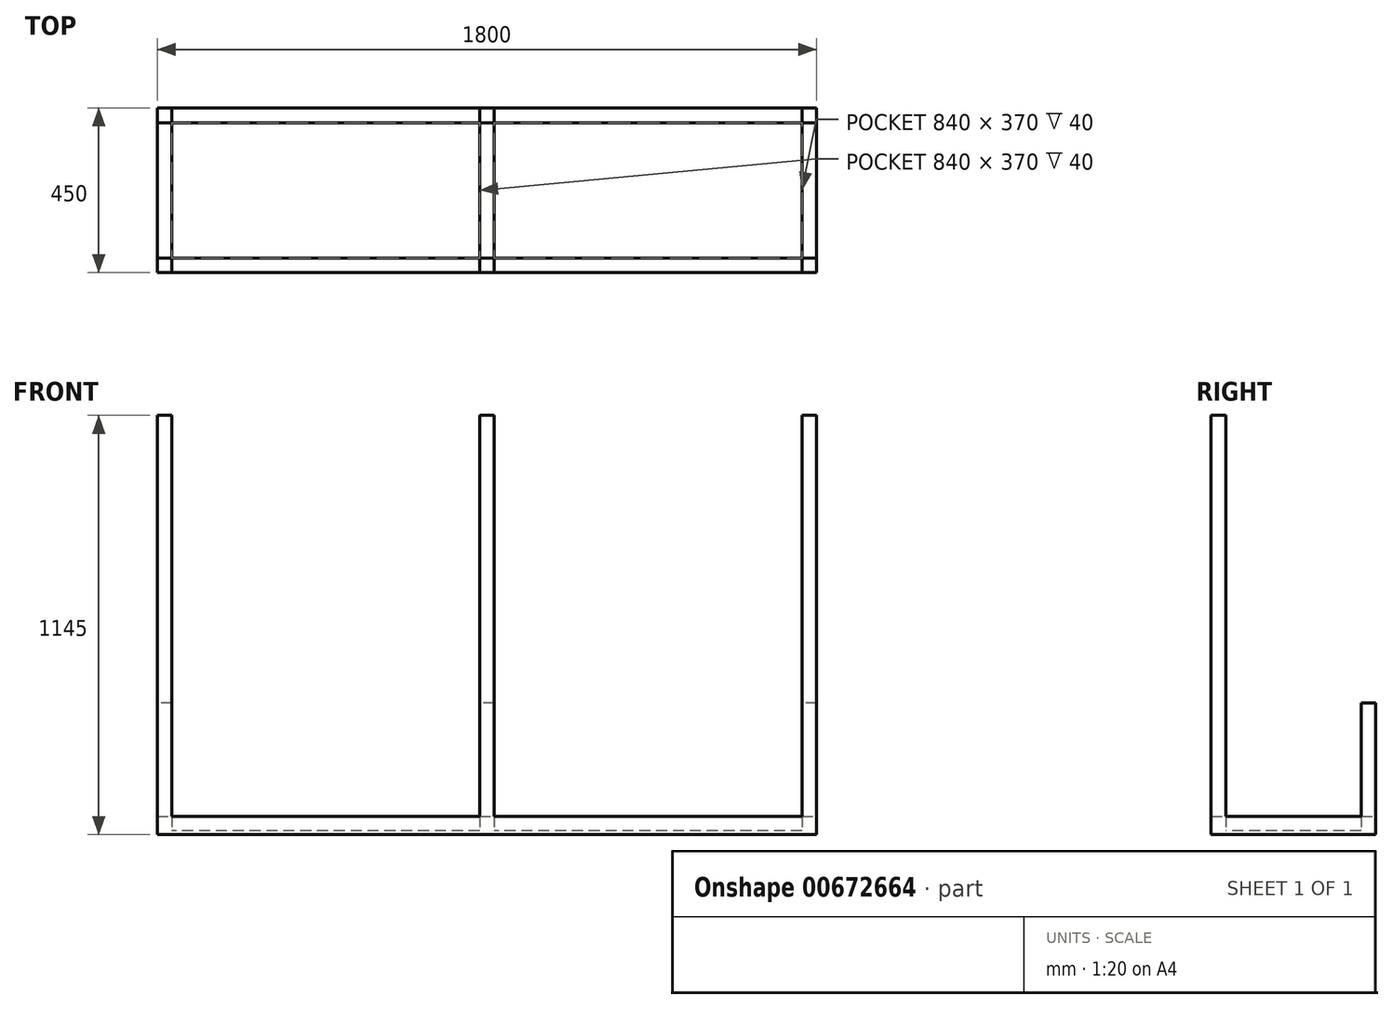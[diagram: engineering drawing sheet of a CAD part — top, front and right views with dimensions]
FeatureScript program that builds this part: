
annotation { "Feature Type Name" : "Feature", "Feature Type Description" : "" }
export const myFeature = defineFeature(function(context is Context, id is Id, definition is map)
    precondition{}
    {
        {
            var Q0;
            Q0=qCreatedBy(makeId("Top.planeOp"),FACE);
            var sketch = newSketch(context, id + "F0", { "sketchPlane" : qUnion([Q0])});
            skLineSegment(sketch, "E0.bottom", {"start": v(900, -225) * mm, "end": v(-900, -225) * mm});
            skLineSegment(sketch, "E0.top", {"start": v(900, 225) * mm, "end": v(-900, 225) * mm});
            skLineSegment(sketch, "E0.left", {"start": v(900, -225) * mm, "end": v(900, 225) * mm});
            skLineSegment(sketch, "E0.right", {"start": v(-900, -225) * mm, "end": v(-900, 225) * mm});
            skPoint(sketch, "E0.middle", {"position": v(0, 0) * mm});
            skSolve(sketch);
        }
        {
            var Q0;
            Q0=makeQuery(id+"F0.imprint","IMPRINT",FACE,{"disambiguationData":[TD([[makeQuery(id+"F0.imprint","IMPRINT",EDGE,{"derivedFrom":sQuery(id+"F0.wireOp",EDGE,"E0.bottom")}),-1.0]])]});
            extrude(context, id + "F1", {"entities" : qUnion([Q0]), "depth" : 10 * mm, "offsetDistance" : 25 * mm});
        }
        {
            var Q0;
            Q0=makeQuery(id+"F1.opExtrude","CAP_FACE",FACE,{"disambiguationData":[OSD([sQuery(id+"F0.wireOp",EDGE,"E0.bottom"),sQuery(id+"F0.wireOp",EDGE,"E0.top"),sQuery(id+"F0.wireOp",EDGE,"E0.left"),sQuery(id+"F0.wireOp",EDGE,"E0.right")])],"isStart":false});
            var sketch = newSketch(context, id + "F2", { "sketchPlane" : qUnion([Q0])});
            skLineSegment(sketch, "E1.bottom", {"start": v(-900, 225) * mm, "end": v(-860, 225) * mm});
            skLineSegment(sketch, "E1.top", {"start": v(-900, -225) * mm, "end": v(-860, -225) * mm});
            skLineSegment(sketch, "E1.left", {"start": v(-900, 225) * mm, "end": v(-900, -225) * mm});
            skLineSegment(sketch, "E1.right", {"start": v(-860, 225) * mm, "end": v(-860, -225) * mm});
            skSolve(sketch);
        }
        {
            var Q0;
            Q0=makeQuery(id+"F2.imprint","IMPRINT",FACE,{"disambiguationData":[TD([[makeQuery(id+"F2.imprint","IMPRINT",EDGE,{"derivedFrom":sQuery(id+"F2.wireOp",EDGE,"E1.bottom")}),1.0]])]});
            extrude(context, id + "F3", {"entities" : qUnion([Q0]), "operationType" : NewBodyOperationType.ADD, "depth" : 40 * mm, "offsetDistance" : 25 * mm});
        }
        {
            var Q0;
            Q0=makeQuery(id+"F1.opExtrude","CAP_FACE",FACE,{"disambiguationData":[OSD([sQuery(id+"F0.wireOp",EDGE,"E0.bottom"),sQuery(id+"F0.wireOp",EDGE,"E0.top"),sQuery(id+"F0.wireOp",EDGE,"E0.left"),sQuery(id+"F0.wireOp",EDGE,"E0.right")])],"isStart":false});
            var sketch = newSketch(context, id + "F4", { "sketchPlane" : qUnion([Q0])});
            skLineSegment(sketch, "E2.bottom", {"start": v(900, 225) * mm, "end": v(860, 225) * mm});
            skLineSegment(sketch, "E2.top", {"start": v(900, -225) * mm, "end": v(860, -225) * mm});
            skLineSegment(sketch, "E2.left", {"start": v(900, 225) * mm, "end": v(900, -225) * mm});
            skLineSegment(sketch, "E2.right", {"start": v(860, 225) * mm, "end": v(860, -225) * mm});
            skSolve(sketch);
        }
        {
            var Q0;
            Q0=makeQuery(id+"F4.imprint","IMPRINT",FACE,{"disambiguationData":[TD([[makeQuery(id+"F4.imprint","IMPRINT",EDGE,{"derivedFrom":sQuery(id+"F4.wireOp",EDGE,"E2.bottom")}),1.0]])]});
            extrude(context, id + "F5", {"entities" : qUnion([Q0]), "operationType" : NewBodyOperationType.ADD, "depth" : 40 * mm, "offsetDistance" : 25 * mm});
        }
        {
            var Q0;
            Q0=makeQuery(id+"F1.opExtrude","CAP_FACE",FACE,{"disambiguationData":[OSD([sQuery(id+"F0.wireOp",EDGE,"E0.bottom"),sQuery(id+"F0.wireOp",EDGE,"E0.top"),sQuery(id+"F0.wireOp",EDGE,"E0.left"),sQuery(id+"F0.wireOp",EDGE,"E0.right")])],"isStart":false});
            var sketch = newSketch(context, id + "F6", { "sketchPlane" : qUnion([Q0])});
            skLineSegment(sketch, "E3.bottom", {"start": v(-20, 185) * mm, "end": v(20, 185) * mm});
            skLineSegment(sketch, "E3.top", {"start": v(-20, -185) * mm, "end": v(20, -185) * mm});
            skLineSegment(sketch, "E3.left", {"start": v(-20, 185) * mm, "end": v(-20, -185) * mm});
            skLineSegment(sketch, "E3.right", {"start": v(20, 185) * mm, "end": v(20, -185) * mm});
            skPoint(sketch, "E3.middle", {"position": v(0, 0) * mm});
            skSolve(sketch);
        }
        {
            var Q0;
            Q0=makeQuery(id+"F6.imprint","IMPRINT",FACE,{"disambiguationData":[TD([[makeQuery(id+"F6.imprint","IMPRINT",EDGE,{"derivedFrom":sQuery(id+"F6.wireOp",EDGE,"E3.bottom")}),-1.0]])]});
            extrude(context, id + "F7", {"entities" : qUnion([Q0]), "operationType" : NewBodyOperationType.ADD, "depth" : 40 * mm, "offsetDistance" : 25 * mm});
        }
        {
            var Q0;
            Q0=makeQuery(id+"F1.opExtrude","CAP_FACE",FACE,{"disambiguationData":[OSD([sQuery(id+"F0.wireOp",EDGE,"E0.bottom"),sQuery(id+"F0.wireOp",EDGE,"E0.top"),sQuery(id+"F0.wireOp",EDGE,"E0.left"),sQuery(id+"F0.wireOp",EDGE,"E0.right")])],"isStart":false});
            var sketch = newSketch(context, id + "F8", { "sketchPlane" : qUnion([Q0])});
            skLineSegment(sketch, "E4.bottom", {"start": v(860, -225) * mm, "end": v(-860, -225) * mm});
            skLineSegment(sketch, "E4.top", {"start": v(860, -185) * mm, "end": v(-860, -185) * mm});
            skLineSegment(sketch, "E4.left", {"start": v(860, -225) * mm, "end": v(860, -185) * mm});
            skLineSegment(sketch, "E4.right", {"start": v(-860, -225) * mm, "end": v(-860, -185) * mm});
            skSolve(sketch);
        }
        {
            var Q0;
            Q0=makeQuery(id+"F8.imprint","IMPRINT",FACE,{"disambiguationData":[TD([[makeQuery(id+"F8.imprint","IMPRINT",EDGE,{"derivedFrom":sQuery(id+"F8.wireOp",EDGE,"E4.bottom")}),-1.0]])]});
            extrude(context, id + "F9", {"entities" : qUnion([Q0]), "operationType" : NewBodyOperationType.ADD, "depth" : 40 * mm, "offsetDistance" : 25 * mm});
        }
        {
            var Q0;
            Q0=makeQuery(id+"F1.opExtrude","CAP_FACE",FACE,{"disambiguationData":[OSD([sQuery(id+"F0.wireOp",EDGE,"E0.bottom"),sQuery(id+"F0.wireOp",EDGE,"E0.top"),sQuery(id+"F0.wireOp",EDGE,"E0.left"),sQuery(id+"F0.wireOp",EDGE,"E0.right")])],"isStart":false});
            var sketch = newSketch(context, id + "F10", { "sketchPlane" : qUnion([Q0])});
            skLineSegment(sketch, "E5.bottom", {"start": v(860, 225) * mm, "end": v(-860, 225) * mm});
            skLineSegment(sketch, "E5.top", {"start": v(860, 185) * mm, "end": v(-860, 185) * mm});
            skLineSegment(sketch, "E5.left", {"start": v(860, 225) * mm, "end": v(860, 185) * mm});
            skLineSegment(sketch, "E5.right", {"start": v(-860, 225) * mm, "end": v(-860, 185) * mm});
            skSolve(sketch);
        }
        {
            var Q0;
            Q0=makeQuery(id+"F10.imprint","IMPRINT",FACE,{"disambiguationData":[TD([[makeQuery(id+"F10.imprint","IMPRINT",EDGE,{"derivedFrom":sQuery(id+"F10.wireOp",EDGE,"E5.bottom")}),1.0]])]});
            extrude(context, id + "F11", {"entities" : qUnion([Q0]), "operationType" : NewBodyOperationType.ADD, "depth" : 40 * mm, "offsetDistance" : 25 * mm});
        }
        {
            var Q0;
            Q0=makeQuery(id+"F11.boolean.opBoolean","MERGE",FACE,{"derivedFrom":[makeQuery(id+"F9.boolean.opBoolean","MERGE",FACE,{"derivedFrom":[makeQuery(id+"F3.opExtrude","CAP_FACE",FACE,{"disambiguationData":[OSD([sQuery(id+"F2.wireOp",EDGE,"E1.bottom"),sQuery(id+"F2.wireOp",EDGE,"E1.top"),sQuery(id+"F2.wireOp",EDGE,"E1.left"),sQuery(id+"F2.wireOp",EDGE,"E1.right")])],"isStart":false}),makeQuery(id+"F5.opExtrude","CAP_FACE",FACE,{"disambiguationData":[OSD([sQuery(id+"F4.wireOp",EDGE,"E2.bottom"),sQuery(id+"F4.wireOp",EDGE,"E2.top"),sQuery(id+"F4.wireOp",EDGE,"E2.left"),sQuery(id+"F4.wireOp",EDGE,"E2.right")])],"isStart":false}),makeQuery(id+"F7.opExtrude","CAP_FACE",FACE,{"disambiguationData":[OSD([sQuery(id+"F6.wireOp",EDGE,"E3.bottom"),sQuery(id+"F6.wireOp",EDGE,"E3.top"),sQuery(id+"F6.wireOp",EDGE,"E3.left"),sQuery(id+"F6.wireOp",EDGE,"E3.right")])],"isStart":false}),makeQuery(id+"F9.opExtrude","CAP_FACE",FACE,{"disambiguationData":[OSD([sQuery(id+"F8.wireOp",EDGE,"E4.bottom"),sQuery(id+"F8.wireOp",EDGE,"E4.top"),sQuery(id+"F8.wireOp",EDGE,"E4.left"),sQuery(id+"F8.wireOp",EDGE,"E4.right")])],"isStart":false})]}),makeQuery(id+"F11.opExtrude","CAP_FACE",FACE,{"disambiguationData":[OSD([sQuery(id+"F10.wireOp",EDGE,"E5.bottom"),sQuery(id+"F10.wireOp",EDGE,"E5.top"),sQuery(id+"F10.wireOp",EDGE,"E5.left"),sQuery(id+"F10.wireOp",EDGE,"E5.right")])],"isStart":false})]});
            var sketch = newSketch(context, id + "F12", { "sketchPlane" : qUnion([Q0])});
            skLineSegment(sketch, "E6.bottom", {"start": v(-900, -225) * mm, "end": v(-860, -225) * mm});
            skLineSegment(sketch, "E6.top", {"start": v(-900, -185) * mm, "end": v(-860, -185) * mm});
            skLineSegment(sketch, "E6.left", {"start": v(-900, -225) * mm, "end": v(-900, -185) * mm});
            skLineSegment(sketch, "E6.right", {"start": v(-860, -225) * mm, "end": v(-860, -185) * mm});
            skSolve(sketch);
        }
        {
            var Q0;
            Q0=makeQuery(id+"F12.imprint","IMPRINT",FACE,{"disambiguationData":[TD([[makeQuery(id+"F12.imprint","IMPRINT",EDGE,{"derivedFrom":sQuery(id+"F12.wireOp",EDGE,"E6.bottom")}),-1.0]])]});
            extrude(context, id + "F13", {"entities" : qUnion([Q0]), "operationType" : NewBodyOperationType.ADD, "depth" : 1095 * mm, "offsetDistance" : 25 * mm});
        }
        {
            var Q0;
            Q0=makeQuery(id+"F11.boolean.opBoolean","MERGE",FACE,{"derivedFrom":[makeQuery(id+"F9.boolean.opBoolean","MERGE",FACE,{"derivedFrom":[makeQuery(id+"F3.opExtrude","CAP_FACE",FACE,{"disambiguationData":[OSD([sQuery(id+"F2.wireOp",EDGE,"E1.bottom"),sQuery(id+"F2.wireOp",EDGE,"E1.top"),sQuery(id+"F2.wireOp",EDGE,"E1.left"),sQuery(id+"F2.wireOp",EDGE,"E1.right")])],"isStart":false}),makeQuery(id+"F5.opExtrude","CAP_FACE",FACE,{"disambiguationData":[OSD([sQuery(id+"F4.wireOp",EDGE,"E2.bottom"),sQuery(id+"F4.wireOp",EDGE,"E2.top"),sQuery(id+"F4.wireOp",EDGE,"E2.left"),sQuery(id+"F4.wireOp",EDGE,"E2.right")])],"isStart":false}),makeQuery(id+"F7.opExtrude","CAP_FACE",FACE,{"disambiguationData":[OSD([sQuery(id+"F6.wireOp",EDGE,"E3.bottom"),sQuery(id+"F6.wireOp",EDGE,"E3.top"),sQuery(id+"F6.wireOp",EDGE,"E3.left"),sQuery(id+"F6.wireOp",EDGE,"E3.right")])],"isStart":false}),makeQuery(id+"F9.opExtrude","CAP_FACE",FACE,{"disambiguationData":[OSD([sQuery(id+"F8.wireOp",EDGE,"E4.bottom"),sQuery(id+"F8.wireOp",EDGE,"E4.top"),sQuery(id+"F8.wireOp",EDGE,"E4.left"),sQuery(id+"F8.wireOp",EDGE,"E4.right")])],"isStart":false})]}),makeQuery(id+"F11.opExtrude","CAP_FACE",FACE,{"disambiguationData":[OSD([sQuery(id+"F10.wireOp",EDGE,"E5.bottom"),sQuery(id+"F10.wireOp",EDGE,"E5.top"),sQuery(id+"F10.wireOp",EDGE,"E5.left"),sQuery(id+"F10.wireOp",EDGE,"E5.right")])],"isStart":false})]});
            var sketch = newSketch(context, id + "F14", { "sketchPlane" : qUnion([Q0])});
            skLineSegment(sketch, "E7.bottom", {"start": v(-20, -185) * mm, "end": v(20, -185) * mm});
            skLineSegment(sketch, "E7.top", {"start": v(-20, -225) * mm, "end": v(20, -225) * mm});
            skLineSegment(sketch, "E7.left", {"start": v(-20, -185) * mm, "end": v(-20, -225) * mm});
            skLineSegment(sketch, "E7.right", {"start": v(20, -185) * mm, "end": v(20, -225) * mm});
            skSolve(sketch);
        }
        {
            var Q0;
            Q0=makeQuery(id+"F14.imprint","IMPRINT",FACE,{"disambiguationData":[TD([[makeQuery(id+"F14.imprint","IMPRINT",EDGE,{"derivedFrom":sQuery(id+"F14.wireOp",EDGE,"E7.bottom")}),-1.0]])]});
            extrude(context, id + "F15", {"entities" : qUnion([Q0]), "operationType" : NewBodyOperationType.ADD, "depth" : 1095 * mm, "offsetDistance" : 25 * mm});
        }
        {
            var Q0;
            {var subQ0=sQuery(id+"F10.wireOp",EDGE,"E5.bottom");var subQ1=sQuery(id+"F10.wireOp",EDGE,"E5.top");var subQ2=makeQuery(id+"F11.opExtrude","CAP_FACE",FACE,{"disambiguationData":[OSD([subQ0,subQ1,sQuery(id+"F10.wireOp",EDGE,"E5.left"),sQuery(id+"F10.wireOp",EDGE,"E5.right")])],"isStart":false});var subQ3=sQuery(id+"F6.wireOp",EDGE,"E3.right");var subQ4=sQuery(id+"F6.wireOp",EDGE,"E3.left");var subQ5=sQuery(id+"F8.wireOp",EDGE,"E4.top");var subQ6=sQuery(id+"F8.wireOp",EDGE,"E4.bottom");var subQ7=makeQuery(id+"F9.opExtrude","CAP_FACE",FACE,{"disambiguationData":[OSD([subQ6,subQ5,sQuery(id+"F8.wireOp",EDGE,"E4.left"),sQuery(id+"F8.wireOp",EDGE,"E4.right")])],"isStart":false});var subQ8=sQuery(id+"F4.wireOp",EDGE,"E2.right");var subQ9=sQuery(id+"F4.wireOp",EDGE,"E2.left");var subQ10=sQuery(id+"F4.wireOp",EDGE,"E2.top");var subQ11=sQuery(id+"F4.wireOp",EDGE,"E2.bottom");var subQ12=makeQuery(id+"F5.opExtrude","CAP_FACE",FACE,{"disambiguationData":[OSD([subQ11,subQ10,subQ9,subQ8])],"isStart":false});var subQ13=sQuery(id+"F2.wireOp",EDGE,"E1.top");var subQ14=sQuery(id+"F2.wireOp",EDGE,"E1.right");var subQ15=sQuery(id+"F2.wireOp",EDGE,"E1.left");var subQ16=sQuery(id+"F2.wireOp",EDGE,"E1.bottom");var subQ17=makeQuery(id+"F3.opExtrude","CAP_FACE",FACE,{"disambiguationData":[OSD([subQ16,subQ13,subQ15,subQ14])],"isStart":false});var subQ18=makeQuery(id+"F7.opExtrude","CAP_FACE",FACE,{"disambiguationData":[OSD([sQuery(id+"F6.wireOp",EDGE,"E3.bottom"),sQuery(id+"F6.wireOp",EDGE,"E3.top"),subQ4,subQ3])],"isStart":false});Q0=makeQuery(id+"F15.boolean.opBoolean","SPLIT",FACE,{"disambiguationData":[TD([makeQuery(id+"F1.opExtrude","SWEPT_FACE",FACE,{"disambiguationData":[OSD([sQuery(id+"F0.wireOp",EDGE,"E0.bottom")])]}),makeQuery(id+"F1.opExtrude","SWEPT_FACE",FACE,{"disambiguationData":[OSD([sQuery(id+"F0.wireOp",EDGE,"E0.top")])]}),makeQuery(id+"F1.opExtrude","SWEPT_FACE",FACE,{"disambiguationData":[OSD([sQuery(id+"F0.wireOp",EDGE,"E0.left")])]}),makeQuery(id+"F1.opExtrude","SWEPT_FACE",FACE,{"disambiguationData":[OSD([sQuery(id+"F0.wireOp",EDGE,"E0.right")])]}),makeQuery(id+"F3.opExtrude","SWEPT_FACE",FACE,{"disambiguationData":[OSD([subQ16])]}),subQ17,makeQuery(id+"F3.opExtrude","SWEPT_FACE",FACE,{"disambiguationData":[OSD([subQ13])]}),makeQuery(id+"F3.opExtrude","SWEPT_FACE",FACE,{"disambiguationData":[OSD([subQ15])]}),makeQuery(id+"F3.opExtrude","SWEPT_FACE",FACE,{"disambiguationData":[OSD([subQ14])]}),makeQuery(id+"F5.opExtrude","SWEPT_FACE",FACE,{"disambiguationData":[OSD([subQ11])]}),subQ12,makeQuery(id+"F5.opExtrude","SWEPT_FACE",FACE,{"disambiguationData":[OSD([subQ10])]}),makeQuery(id+"F5.opExtrude","SWEPT_FACE",FACE,{"disambiguationData":[OSD([subQ9])]}),makeQuery(id+"F5.opExtrude","SWEPT_FACE",FACE,{"disambiguationData":[OSD([subQ8])]}),subQ18,makeQuery(id+"F7.opExtrude","SWEPT_FACE",FACE,{"disambiguationData":[OSD([subQ4])]}),makeQuery(id+"F7.opExtrude","SWEPT_FACE",FACE,{"disambiguationData":[OSD([subQ3])]}),makeQuery(id+"F9.opExtrude","SWEPT_FACE",FACE,{"disambiguationData":[OSD([subQ6])]}),subQ7,makeQuery(id+"F9.opExtrude","SWEPT_FACE",FACE,{"disambiguationData":[OSD([subQ5])]}),makeQuery(id+"F11.opExtrude","SWEPT_FACE",FACE,{"disambiguationData":[OSD([subQ0])]}),subQ2,makeQuery(id+"F11.opExtrude","SWEPT_FACE",FACE,{"disambiguationData":[OSD([subQ1])]}),makeQuery(id+"F13.opExtrude","SWEPT_FACE",FACE,{"disambiguationData":[OSD([sQuery(id+"F12.wireOp",EDGE,"E6.bottom")])]}),makeQuery(id+"F13.opExtrude","SWEPT_FACE",FACE,{"disambiguationData":[OSD([sQuery(id+"F12.wireOp",EDGE,"E6.top")])]}),makeQuery(id+"F13.opExtrude","SWEPT_FACE",FACE,{"disambiguationData":[OSD([sQuery(id+"F12.wireOp",EDGE,"E6.left")])]}),makeQuery(id+"F13.opExtrude","SWEPT_FACE",FACE,{"disambiguationData":[OSD([sQuery(id+"F12.wireOp",EDGE,"E6.right")])]}),makeQuery(id+"F15.opExtrude","SWEPT_FACE",FACE,{"disambiguationData":[OSD([sQuery(id+"F14.wireOp",EDGE,"E7.bottom")])]}),makeQuery(id+"F15.opExtrude","SWEPT_FACE",FACE,{"disambiguationData":[OSD([sQuery(id+"F14.wireOp",EDGE,"E7.top")])]}),makeQuery(id+"F15.opExtrude","SWEPT_FACE",FACE,{"disambiguationData":[OSD([sQuery(id+"F14.wireOp",EDGE,"E7.left")])]}),makeQuery(id+"F15.opExtrude","SWEPT_FACE",FACE,{"disambiguationData":[OSD([sQuery(id+"F14.wireOp",EDGE,"E7.right")])]})])],"derivedFrom":makeQuery(id+"F11.boolean.opBoolean","MERGE",FACE,{"derivedFrom":[makeQuery(id+"F9.boolean.opBoolean","MERGE",FACE,{"derivedFrom":[subQ17,subQ12,subQ18,subQ7]}),subQ2]})});}
            var sketch = newSketch(context, id + "F16", { "sketchPlane" : qUnion([Q0])});
            skLineSegment(sketch, "E8.bottom", {"start": v(900, -225) * mm, "end": v(860, -225) * mm});
            skLineSegment(sketch, "E8.top", {"start": v(900, -185) * mm, "end": v(860, -185) * mm});
            skLineSegment(sketch, "E8.left", {"start": v(900, -225) * mm, "end": v(900, -185) * mm});
            skLineSegment(sketch, "E8.right", {"start": v(860, -225) * mm, "end": v(860, -185) * mm});
            skSolve(sketch);
        }
        {
            var Q0;
            Q0=makeQuery(id+"F16.imprint","IMPRINT",FACE,{"disambiguationData":[TD([[makeQuery(id+"F16.imprint","IMPRINT",EDGE,{"derivedFrom":sQuery(id+"F16.wireOp",EDGE,"E8.bottom")}),-1.0]])]});
            extrude(context, id + "F17", {"entities" : qUnion([Q0]), "operationType" : NewBodyOperationType.ADD, "depth" : 1095 * mm, "offsetDistance" : 25 * mm});
        }
        {
            var Q0;
            {var subQ0=sQuery(id+"F10.wireOp",EDGE,"E5.top");var subQ1=makeQuery(id+"F11.opExtrude","SWEPT_FACE",FACE,{"disambiguationData":[OSD([subQ0])]});var subQ2=sQuery(id+"F10.wireOp",EDGE,"E5.bottom");var subQ3=makeQuery(id+"F11.opExtrude","SWEPT_FACE",FACE,{"disambiguationData":[OSD([subQ2])]});var subQ4=makeQuery(id+"F1.opExtrude","SWEPT_FACE",FACE,{"disambiguationData":[OSD([sQuery(id+"F0.wireOp",EDGE,"E0.right")])]});var subQ5=sQuery(id+"F8.wireOp",EDGE,"E4.top");var subQ6=makeQuery(id+"F9.opExtrude","SWEPT_FACE",FACE,{"disambiguationData":[OSD([subQ5])]});var subQ7=makeQuery(id+"F11.opExtrude","CAP_FACE",FACE,{"disambiguationData":[OSD([subQ2,subQ0,sQuery(id+"F10.wireOp",EDGE,"E5.left"),sQuery(id+"F10.wireOp",EDGE,"E5.right")])],"isStart":false});var subQ8=sQuery(id+"F6.wireOp",EDGE,"E3.right");var subQ9=makeQuery(id+"F7.opExtrude","SWEPT_FACE",FACE,{"disambiguationData":[OSD([subQ8])]});var subQ10=sQuery(id+"F6.wireOp",EDGE,"E3.left");var subQ11=makeQuery(id+"F7.opExtrude","SWEPT_FACE",FACE,{"disambiguationData":[OSD([subQ10])]});var subQ12=sQuery(id+"F8.wireOp",EDGE,"E4.bottom");var subQ13=makeQuery(id+"F9.opExtrude","CAP_FACE",FACE,{"disambiguationData":[OSD([subQ12,subQ5,sQuery(id+"F8.wireOp",EDGE,"E4.left"),sQuery(id+"F8.wireOp",EDGE,"E4.right")])],"isStart":false});var subQ14=sQuery(id+"F4.wireOp",EDGE,"E2.right");var subQ15=makeQuery(id+"F5.opExtrude","SWEPT_FACE",FACE,{"disambiguationData":[OSD([subQ14])]});var subQ16=makeQuery(id+"F13.opExtrude","SWEPT_FACE",FACE,{"disambiguationData":[OSD([sQuery(id+"F12.wireOp",EDGE,"E6.right")])]});var subQ17=sQuery(id+"F2.wireOp",EDGE,"E1.left");var subQ18=makeQuery(id+"F3.opExtrude","SWEPT_FACE",FACE,{"disambiguationData":[OSD([subQ17])]});var subQ19=makeQuery(id+"F13.opExtrude","SWEPT_FACE",FACE,{"disambiguationData":[OSD([sQuery(id+"F12.wireOp",EDGE,"E6.left")])]});var subQ20=makeQuery(id+"F1.opExtrude","SWEPT_FACE",FACE,{"disambiguationData":[OSD([sQuery(id+"F0.wireOp",EDGE,"E0.left")])]});var subQ21=sQuery(id+"F2.wireOp",EDGE,"E1.bottom");var subQ22=makeQuery(id+"F3.opExtrude","SWEPT_FACE",FACE,{"disambiguationData":[OSD([subQ21])]});var subQ23=makeQuery(id+"F13.opExtrude","SWEPT_FACE",FACE,{"disambiguationData":[OSD([sQuery(id+"F12.wireOp",EDGE,"E6.top")])]});var subQ24=makeQuery(id+"F1.opExtrude","SWEPT_FACE",FACE,{"disambiguationData":[OSD([sQuery(id+"F0.wireOp",EDGE,"E0.top")])]});var subQ25=sQuery(id+"F2.wireOp",EDGE,"E1.right");var subQ26=sQuery(id+"F2.wireOp",EDGE,"E1.top");var subQ27=makeQuery(id+"F3.opExtrude","CAP_FACE",FACE,{"disambiguationData":[OSD([subQ21,subQ26,subQ17,subQ25])],"isStart":false});var subQ28=makeQuery(id+"F7.opExtrude","CAP_FACE",FACE,{"disambiguationData":[OSD([sQuery(id+"F6.wireOp",EDGE,"E3.bottom"),sQuery(id+"F6.wireOp",EDGE,"E3.top"),subQ10,subQ8])],"isStart":false});var subQ29=makeQuery(id+"F3.opExtrude","SWEPT_FACE",FACE,{"disambiguationData":[OSD([subQ25])]});var subQ30=sQuery(id+"F4.wireOp",EDGE,"E2.bottom");var subQ31=makeQuery(id+"F5.opExtrude","SWEPT_FACE",FACE,{"disambiguationData":[OSD([subQ30])]});var subQ32=sQuery(id+"F4.wireOp",EDGE,"E2.left");var subQ33=sQuery(id+"F4.wireOp",EDGE,"E2.top");var subQ34=makeQuery(id+"F5.opExtrude","CAP_FACE",FACE,{"disambiguationData":[OSD([subQ30,subQ33,subQ32,subQ14])],"isStart":false});var subQ35=makeQuery(id+"F5.opExtrude","SWEPT_FACE",FACE,{"disambiguationData":[OSD([subQ32])]});var subQ36=makeQuery(id+"F15.opExtrude","SWEPT_FACE",FACE,{"disambiguationData":[OSD([sQuery(id+"F14.wireOp",EDGE,"E7.bottom")])]});var subQ37=makeQuery(id+"F15.opExtrude","SWEPT_FACE",FACE,{"disambiguationData":[OSD([sQuery(id+"F14.wireOp",EDGE,"E7.left")])]});var subQ38=makeQuery(id+"F15.opExtrude","SWEPT_FACE",FACE,{"disambiguationData":[OSD([sQuery(id+"F14.wireOp",EDGE,"E7.right")])]});Q0=makeQuery(id+"F17.boolean.opBoolean","SPLIT",FACE,{"disambiguationData":[TD([subQ24])],"derivedFrom":makeQuery(id+"F15.boolean.opBoolean","SPLIT",FACE,{"disambiguationData":[TD([makeQuery(id+"F1.opExtrude","SWEPT_FACE",FACE,{"disambiguationData":[OSD([sQuery(id+"F0.wireOp",EDGE,"E0.bottom")])]}),subQ24,subQ20,subQ4,subQ22,subQ27,makeQuery(id+"F3.opExtrude","SWEPT_FACE",FACE,{"disambiguationData":[OSD([subQ26])]}),subQ18,subQ29,subQ31,subQ34,makeQuery(id+"F5.opExtrude","SWEPT_FACE",FACE,{"disambiguationData":[OSD([subQ33])]}),subQ35,subQ15,subQ28,subQ11,subQ9,makeQuery(id+"F9.opExtrude","SWEPT_FACE",FACE,{"disambiguationData":[OSD([subQ12])]}),subQ13,subQ6,subQ3,subQ7,subQ1,makeQuery(id+"F13.opExtrude","SWEPT_FACE",FACE,{"disambiguationData":[OSD([sQuery(id+"F12.wireOp",EDGE,"E6.bottom")])]}),subQ23,subQ19,subQ16,subQ36,makeQuery(id+"F15.opExtrude","SWEPT_FACE",FACE,{"disambiguationData":[OSD([sQuery(id+"F14.wireOp",EDGE,"E7.top")])]}),subQ37,subQ38])],"derivedFrom":makeQuery(id+"F11.boolean.opBoolean","MERGE",FACE,{"derivedFrom":[makeQuery(id+"F9.boolean.opBoolean","MERGE",FACE,{"derivedFrom":[subQ27,subQ34,subQ28,subQ13]}),subQ7]})})});}
            var sketch = newSketch(context, id + "F18", { "sketchPlane" : qUnion([Q0])});
            skLineSegment(sketch, "E9.bottom", {"start": v(-900, 225) * mm, "end": v(-860, 225) * mm});
            skLineSegment(sketch, "E9.top", {"start": v(-900, 185) * mm, "end": v(-860, 185) * mm});
            skLineSegment(sketch, "E9.left", {"start": v(-900, 225) * mm, "end": v(-900, 185) * mm});
            skLineSegment(sketch, "E9.right", {"start": v(-860, 225) * mm, "end": v(-860, 185) * mm});
            skSolve(sketch);
        }
        {
            var Q0;
            Q0=makeQuery(id+"F18.imprint","IMPRINT",FACE,{"disambiguationData":[TD([[makeQuery(id+"F18.imprint","IMPRINT",EDGE,{"derivedFrom":sQuery(id+"F18.wireOp",EDGE,"E9.bottom")}),1.0]])]});
            extrude(context, id + "F19", {"entities" : qUnion([Q0]), "operationType" : NewBodyOperationType.ADD, "depth" : 310 * mm, "offsetDistance" : 25 * mm});
        }
        {
            var Q0;
            {var subQ1=makeQuery(id+"F15.opExtrude","SWEPT_FACE",FACE,{"disambiguationData":[OSD([sQuery(id+"F14.wireOp",EDGE,"E7.right")])]});var subQ2=makeQuery(id+"F15.opExtrude","SWEPT_FACE",FACE,{"disambiguationData":[OSD([sQuery(id+"F14.wireOp",EDGE,"E7.bottom")])]});var subQ3=sQuery(id+"F10.wireOp",EDGE,"E5.top");var subQ4=makeQuery(id+"F11.opExtrude","SWEPT_FACE",FACE,{"disambiguationData":[OSD([subQ3])]});var subQ5=sQuery(id+"F10.wireOp",EDGE,"E5.bottom");var subQ6=makeQuery(id+"F11.opExtrude","SWEPT_FACE",FACE,{"disambiguationData":[OSD([subQ5])]});var subQ7=sQuery(id+"F8.wireOp",EDGE,"E4.top");var subQ8=makeQuery(id+"F9.opExtrude","SWEPT_FACE",FACE,{"disambiguationData":[OSD([subQ7])]});var subQ9=makeQuery(id+"F11.opExtrude","CAP_FACE",FACE,{"disambiguationData":[OSD([subQ5,subQ3,sQuery(id+"F10.wireOp",EDGE,"E5.left"),sQuery(id+"F10.wireOp",EDGE,"E5.right")])],"isStart":false});var subQ10=sQuery(id+"F6.wireOp",EDGE,"E3.right");var subQ11=makeQuery(id+"F7.opExtrude","SWEPT_FACE",FACE,{"disambiguationData":[OSD([subQ10])]});var subQ12=sQuery(id+"F6.wireOp",EDGE,"E3.left");var subQ13=makeQuery(id+"F7.opExtrude","SWEPT_FACE",FACE,{"disambiguationData":[OSD([subQ12])]});var subQ15=sQuery(id+"F2.wireOp",EDGE,"E1.right");var subQ16=sQuery(id+"F2.wireOp",EDGE,"E1.left");var subQ17=sQuery(id+"F2.wireOp",EDGE,"E1.top");var subQ18=sQuery(id+"F2.wireOp",EDGE,"E1.bottom");var subQ19=makeQuery(id+"F3.opExtrude","CAP_FACE",FACE,{"disambiguationData":[OSD([subQ18,subQ17,subQ16,subQ15])],"isStart":false});var subQ20=makeQuery(id+"F1.opExtrude","SWEPT_FACE",FACE,{"disambiguationData":[OSD([sQuery(id+"F0.wireOp",EDGE,"E0.top")])]});var subQ21=makeQuery(id+"F1.opExtrude","SWEPT_FACE",FACE,{"disambiguationData":[OSD([sQuery(id+"F0.wireOp",EDGE,"E0.left")])]});var subQ22=makeQuery(id+"F3.opExtrude","SWEPT_FACE",FACE,{"disambiguationData":[OSD([subQ18])]});var subQ24=makeQuery(id+"F15.opExtrude","SWEPT_FACE",FACE,{"disambiguationData":[OSD([sQuery(id+"F14.wireOp",EDGE,"E7.left")])]});var subQ25=sQuery(id+"F4.wireOp",EDGE,"E2.bottom");var subQ26=makeQuery(id+"F5.opExtrude","SWEPT_FACE",FACE,{"disambiguationData":[OSD([subQ25])]});var subQ27=sQuery(id+"F4.wireOp",EDGE,"E2.right");var subQ28=sQuery(id+"F4.wireOp",EDGE,"E2.left");var subQ29=sQuery(id+"F4.wireOp",EDGE,"E2.top");var subQ30=makeQuery(id+"F5.opExtrude","CAP_FACE",FACE,{"disambiguationData":[OSD([subQ25,subQ29,subQ28,subQ27])],"isStart":false});var subQ31=makeQuery(id+"F5.opExtrude","SWEPT_FACE",FACE,{"disambiguationData":[OSD([subQ28])]});var subQ32=sQuery(id+"F8.wireOp",EDGE,"E4.bottom");var subQ33=makeQuery(id+"F9.opExtrude","CAP_FACE",FACE,{"disambiguationData":[OSD([subQ32,subQ7,sQuery(id+"F8.wireOp",EDGE,"E4.left"),sQuery(id+"F8.wireOp",EDGE,"E4.right")])],"isStart":false});var subQ34=makeQuery(id+"F5.opExtrude","SWEPT_FACE",FACE,{"disambiguationData":[OSD([subQ27])]});var subQ35=makeQuery(id+"F3.opExtrude","SWEPT_FACE",FACE,{"disambiguationData":[OSD([subQ15])]});var subQ36=makeQuery(id+"F7.opExtrude","CAP_FACE",FACE,{"disambiguationData":[OSD([sQuery(id+"F6.wireOp",EDGE,"E3.bottom"),sQuery(id+"F6.wireOp",EDGE,"E3.top"),subQ12,subQ10])],"isStart":false});var subQ37=makeQuery(id+"F1.opExtrude","SWEPT_FACE",FACE,{"disambiguationData":[OSD([sQuery(id+"F0.wireOp",EDGE,"E0.right")])]});var subQ38=makeQuery(id+"F13.opExtrude","SWEPT_FACE",FACE,{"disambiguationData":[OSD([sQuery(id+"F12.wireOp",EDGE,"E6.right")])]});var subQ39=makeQuery(id+"F3.opExtrude","SWEPT_FACE",FACE,{"disambiguationData":[OSD([subQ16])]});var subQ40=makeQuery(id+"F13.opExtrude","SWEPT_FACE",FACE,{"disambiguationData":[OSD([sQuery(id+"F12.wireOp",EDGE,"E6.left")])]});var subQ41=makeQuery(id+"F13.opExtrude","SWEPT_FACE",FACE,{"disambiguationData":[OSD([sQuery(id+"F12.wireOp",EDGE,"E6.top")])]});Q0=makeQuery(id+"F19.boolean.opBoolean","SPLIT",FACE,{"disambiguationData":[TD([subQ20])],"derivedFrom":makeQuery(id+"F17.boolean.opBoolean","SPLIT",FACE,{"disambiguationData":[TD([subQ20])],"derivedFrom":makeQuery(id+"F15.boolean.opBoolean","SPLIT",FACE,{"disambiguationData":[TD([makeQuery(id+"F1.opExtrude","SWEPT_FACE",FACE,{"disambiguationData":[OSD([sQuery(id+"F0.wireOp",EDGE,"E0.bottom")])]}),subQ20,subQ21,subQ37,subQ22,subQ19,makeQuery(id+"F3.opExtrude","SWEPT_FACE",FACE,{"disambiguationData":[OSD([subQ17])]}),subQ39,subQ35,subQ26,subQ30,makeQuery(id+"F5.opExtrude","SWEPT_FACE",FACE,{"disambiguationData":[OSD([subQ29])]}),subQ31,subQ34,subQ36,subQ13,subQ11,makeQuery(id+"F9.opExtrude","SWEPT_FACE",FACE,{"disambiguationData":[OSD([subQ32])]}),subQ33,subQ8,subQ6,subQ9,subQ4,makeQuery(id+"F13.opExtrude","SWEPT_FACE",FACE,{"disambiguationData":[OSD([sQuery(id+"F12.wireOp",EDGE,"E6.bottom")])]}),subQ41,subQ40,subQ38,subQ2,makeQuery(id+"F15.opExtrude","SWEPT_FACE",FACE,{"disambiguationData":[OSD([sQuery(id+"F14.wireOp",EDGE,"E7.top")])]}),subQ24,subQ1])],"derivedFrom":makeQuery(id+"F11.boolean.opBoolean","MERGE",FACE,{"derivedFrom":[makeQuery(id+"F9.boolean.opBoolean","MERGE",FACE,{"derivedFrom":[subQ19,subQ30,subQ36,subQ33]}),subQ9]})})})});}
            var sketch = newSketch(context, id + "F20", { "sketchPlane" : qUnion([Q0])});
            skLineSegment(sketch, "E10.bottom", {"start": v(-20, 185) * mm, "end": v(20, 185) * mm});
            skLineSegment(sketch, "E10.top", {"start": v(-20, 225) * mm, "end": v(20, 225) * mm});
            skLineSegment(sketch, "E10.left", {"start": v(-20, 185) * mm, "end": v(-20, 225) * mm});
            skLineSegment(sketch, "E10.right", {"start": v(20, 185) * mm, "end": v(20, 225) * mm});
            skSolve(sketch);
        }
        {
            var Q0;
            Q0=makeQuery(id+"F20.imprint","IMPRINT",FACE,{"disambiguationData":[TD([[makeQuery(id+"F20.imprint","IMPRINT",EDGE,{"derivedFrom":sQuery(id+"F20.wireOp",EDGE,"E10.bottom")}),1.0]])]});
            extrude(context, id + "F21", {"entities" : qUnion([Q0]), "operationType" : NewBodyOperationType.ADD, "depth" : 310 * mm, "offsetDistance" : 25 * mm});
        }
        {
            var Q0;
            {var subQ0=sQuery(id+"F6.wireOp",EDGE,"E3.right");var subQ1=makeQuery(id+"F7.opExtrude","SWEPT_FACE",FACE,{"disambiguationData":[OSD([subQ0])]});var subQ2=sQuery(id+"F10.wireOp",EDGE,"E5.top");var subQ3=sQuery(id+"F10.wireOp",EDGE,"E5.bottom");var subQ4=makeQuery(id+"F11.opExtrude","CAP_FACE",FACE,{"disambiguationData":[OSD([subQ3,subQ2,sQuery(id+"F10.wireOp",EDGE,"E5.left"),sQuery(id+"F10.wireOp",EDGE,"E5.right")])],"isStart":false});var subQ5=sQuery(id+"F6.wireOp",EDGE,"E3.left");var subQ6=makeQuery(id+"F7.opExtrude","CAP_FACE",FACE,{"disambiguationData":[OSD([sQuery(id+"F6.wireOp",EDGE,"E3.bottom"),sQuery(id+"F6.wireOp",EDGE,"E3.top"),subQ5,subQ0])],"isStart":false});var subQ7=sQuery(id+"F4.wireOp",EDGE,"E2.right");var subQ8=makeQuery(id+"F5.opExtrude","SWEPT_FACE",FACE,{"disambiguationData":[OSD([subQ7])]});var subQ9=sQuery(id+"F8.wireOp",EDGE,"E4.top");var subQ10=sQuery(id+"F8.wireOp",EDGE,"E4.bottom");var subQ11=makeQuery(id+"F9.opExtrude","CAP_FACE",FACE,{"disambiguationData":[OSD([subQ10,subQ9,sQuery(id+"F8.wireOp",EDGE,"E4.left"),sQuery(id+"F8.wireOp",EDGE,"E4.right")])],"isStart":false});var subQ12=sQuery(id+"F4.wireOp",EDGE,"E2.left");var subQ13=makeQuery(id+"F5.opExtrude","SWEPT_FACE",FACE,{"disambiguationData":[OSD([subQ12])]});var subQ14=sQuery(id+"F4.wireOp",EDGE,"E2.top");var subQ15=sQuery(id+"F4.wireOp",EDGE,"E2.bottom");var subQ16=makeQuery(id+"F5.opExtrude","CAP_FACE",FACE,{"disambiguationData":[OSD([subQ15,subQ14,subQ12,subQ7])],"isStart":false});var subQ17=makeQuery(id+"F5.opExtrude","SWEPT_FACE",FACE,{"disambiguationData":[OSD([subQ15])]});var subQ18=sQuery(id+"F2.wireOp",EDGE,"E1.bottom");var subQ19=makeQuery(id+"F3.opExtrude","SWEPT_FACE",FACE,{"disambiguationData":[OSD([subQ18])]});var subQ20=makeQuery(id+"F1.opExtrude","SWEPT_FACE",FACE,{"disambiguationData":[OSD([sQuery(id+"F0.wireOp",EDGE,"E0.left")])]});var subQ21=makeQuery(id+"F1.opExtrude","SWEPT_FACE",FACE,{"disambiguationData":[OSD([sQuery(id+"F0.wireOp",EDGE,"E0.top")])]});var subQ22=sQuery(id+"F2.wireOp",EDGE,"E1.right");var subQ23=sQuery(id+"F2.wireOp",EDGE,"E1.left");var subQ24=sQuery(id+"F2.wireOp",EDGE,"E1.top");var subQ25=makeQuery(id+"F3.opExtrude","CAP_FACE",FACE,{"disambiguationData":[OSD([subQ18,subQ24,subQ23,subQ22])],"isStart":false});var subQ27=makeQuery(id+"F9.opExtrude","SWEPT_FACE",FACE,{"disambiguationData":[OSD([subQ9])]});var subQ28=makeQuery(id+"F11.opExtrude","SWEPT_FACE",FACE,{"disambiguationData":[OSD([subQ3])]});var subQ29=makeQuery(id+"F11.opExtrude","SWEPT_FACE",FACE,{"disambiguationData":[OSD([subQ2])]});var subQ33=makeQuery(id+"F15.opExtrude","SWEPT_FACE",FACE,{"disambiguationData":[OSD([sQuery(id+"F14.wireOp",EDGE,"E7.right")])]});var subQ34=makeQuery(id+"F15.opExtrude","SWEPT_FACE",FACE,{"disambiguationData":[OSD([sQuery(id+"F14.wireOp",EDGE,"E7.bottom")])]});var subQ35=makeQuery(id+"F7.opExtrude","SWEPT_FACE",FACE,{"disambiguationData":[OSD([subQ5])]});var subQ36=makeQuery(id+"F15.opExtrude","SWEPT_FACE",FACE,{"disambiguationData":[OSD([sQuery(id+"F14.wireOp",EDGE,"E7.left")])]});var subQ37=makeQuery(id+"F3.opExtrude","SWEPT_FACE",FACE,{"disambiguationData":[OSD([subQ22])]});var subQ38=makeQuery(id+"F1.opExtrude","SWEPT_FACE",FACE,{"disambiguationData":[OSD([sQuery(id+"F0.wireOp",EDGE,"E0.right")])]});var subQ39=makeQuery(id+"F13.opExtrude","SWEPT_FACE",FACE,{"disambiguationData":[OSD([sQuery(id+"F12.wireOp",EDGE,"E6.right")])]});var subQ40=makeQuery(id+"F3.opExtrude","SWEPT_FACE",FACE,{"disambiguationData":[OSD([subQ23])]});var subQ41=makeQuery(id+"F13.opExtrude","SWEPT_FACE",FACE,{"disambiguationData":[OSD([sQuery(id+"F12.wireOp",EDGE,"E6.left")])]});var subQ42=makeQuery(id+"F13.opExtrude","SWEPT_FACE",FACE,{"disambiguationData":[OSD([sQuery(id+"F12.wireOp",EDGE,"E6.top")])]});Q0=makeQuery(id+"F21.boolean.opBoolean","SPLIT",FACE,{"disambiguationData":[TD([subQ20])],"derivedFrom":makeQuery(id+"F19.boolean.opBoolean","SPLIT",FACE,{"disambiguationData":[TD([subQ21])],"derivedFrom":makeQuery(id+"F17.boolean.opBoolean","SPLIT",FACE,{"disambiguationData":[TD([subQ21])],"derivedFrom":makeQuery(id+"F15.boolean.opBoolean","SPLIT",FACE,{"disambiguationData":[TD([makeQuery(id+"F1.opExtrude","SWEPT_FACE",FACE,{"disambiguationData":[OSD([sQuery(id+"F0.wireOp",EDGE,"E0.bottom")])]}),subQ21,subQ20,subQ38,subQ19,subQ25,makeQuery(id+"F3.opExtrude","SWEPT_FACE",FACE,{"disambiguationData":[OSD([subQ24])]}),subQ40,subQ37,subQ17,subQ16,makeQuery(id+"F5.opExtrude","SWEPT_FACE",FACE,{"disambiguationData":[OSD([subQ14])]}),subQ13,subQ8,subQ6,subQ35,subQ1,makeQuery(id+"F9.opExtrude","SWEPT_FACE",FACE,{"disambiguationData":[OSD([subQ10])]}),subQ11,subQ27,subQ28,subQ4,subQ29,makeQuery(id+"F13.opExtrude","SWEPT_FACE",FACE,{"disambiguationData":[OSD([sQuery(id+"F12.wireOp",EDGE,"E6.bottom")])]}),subQ42,subQ41,subQ39,subQ34,makeQuery(id+"F15.opExtrude","SWEPT_FACE",FACE,{"disambiguationData":[OSD([sQuery(id+"F14.wireOp",EDGE,"E7.top")])]}),subQ36,subQ33])],"derivedFrom":makeQuery(id+"F11.boolean.opBoolean","MERGE",FACE,{"derivedFrom":[makeQuery(id+"F9.boolean.opBoolean","MERGE",FACE,{"derivedFrom":[subQ25,subQ16,subQ6,subQ11]}),subQ4]})})})})});}
            var sketch = newSketch(context, id + "F22", { "sketchPlane" : qUnion([Q0])});
            skLineSegment(sketch, "E11.bottom", {"start": v(860, 185) * mm, "end": v(900, 185) * mm});
            skLineSegment(sketch, "E11.top", {"start": v(860, 225) * mm, "end": v(900, 225) * mm});
            skLineSegment(sketch, "E11.left", {"start": v(860, 185) * mm, "end": v(860, 225) * mm});
            skLineSegment(sketch, "E11.right", {"start": v(900, 185) * mm, "end": v(900, 225) * mm});
            skSolve(sketch);
        }
        {
            var Q0;
            Q0=makeQuery(id+"F22.imprint","IMPRINT",FACE,{"disambiguationData":[TD([[makeQuery(id+"F22.imprint","IMPRINT",EDGE,{"derivedFrom":sQuery(id+"F22.wireOp",EDGE,"E11.bottom")}),1.0]])]});
            extrude(context, id + "F23", {"entities" : qUnion([Q0]), "operationType" : NewBodyOperationType.ADD, "depth" : 310 * mm, "offsetDistance" : 25 * mm});
        }
    });
